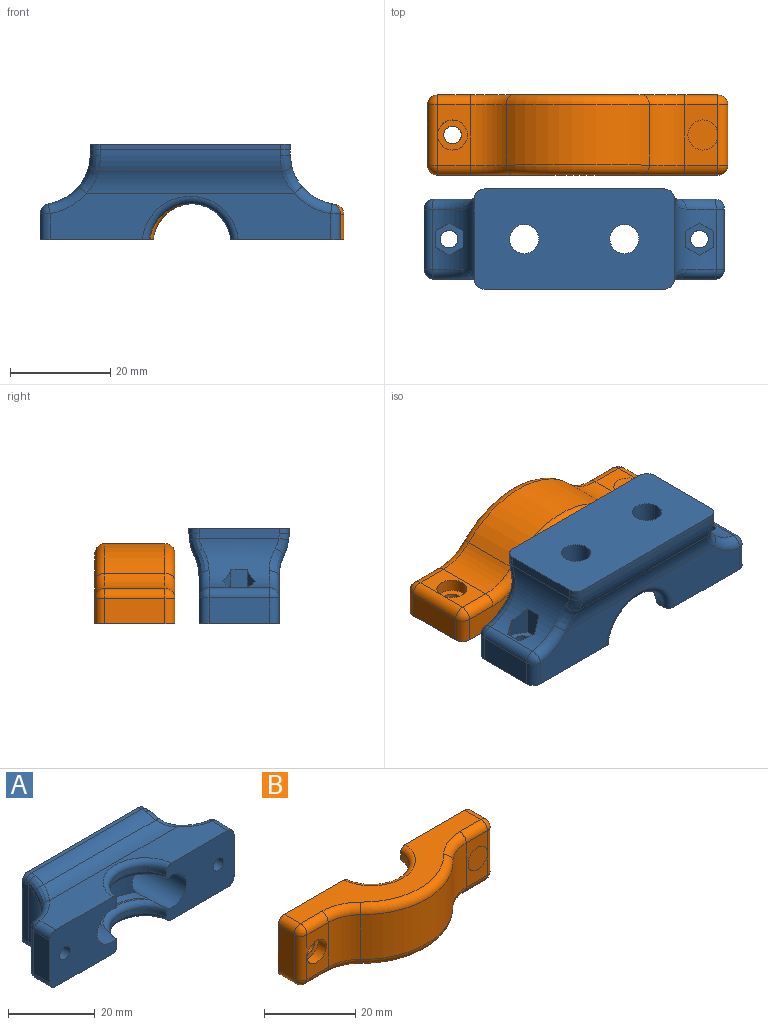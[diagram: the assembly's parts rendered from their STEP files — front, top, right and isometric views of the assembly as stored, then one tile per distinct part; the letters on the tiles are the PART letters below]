
ASSEMBLY  parts=2 mates=1
PART A: 80 faces, bbox 60.1x19.3x20.2 mm
  f0: cylinder r=11.15mm len=12.8mm, axis (0,0,1), area 65.7mm2, adj f5,f6,f76,f78
  f1: plane 14.88x4mm, normal (0,0,1), area 8.4mm2, adj f4,f5,f76,f78
  f2: plane 14.88x4mm, normal (0,0,-1), area 8.4mm2, adj f3,f6,f76,f78
  f3: torus R=9.65mm, axis (0,0,-1), area 49.9mm2, adj f2,f15,f74,f75,f76,f78
  f4: torus R=9.65mm, axis (0,0,1), area 49.9mm2, adj f1,f14,f74,f75,f76,f78
  f5: cone r=10.15mm half-angle=45deg, axis (0,0,1), area 21.1mm2, adj f0,f1,f76,f78
  f6: cone r=11.15mm half-angle=45deg, axis (0,0,-1), area 21.1mm2, adj f0,f2,f76,f78
  f7: cylinder r=2.9mm len=5.8mm, axis (0,1,0), area 72.9mm2, adj f27,f77
  f8: cylinder r=2.9mm len=5.8mm, axis (0,1,0), area 72.9mm2, adj f27,f79
  f9: cylinder r=1.75mm len=5mm, axis (0,1,0), area 55mm2, adj f41,f74
  f10: cylinder r=1.75mm len=5mm, axis (0,1,0), area 55mm2, adj f34,f75
  f11: plane 12x5.17mm, normal (-1,0,0), area 62mm2, adj f19,f20,f59,f75
  f12: plane 12x5.17mm, normal (1,0,0), area 62mm2, adj f21,f22,f67,f74
  f13: plane 56x9.28mm, normal (0,0,-1), area 355mm2, adj f18,f20,f22,f45,f58,f69,f74,f75
  f14: cylinder r=8.15mm len=16.18mm, axis (0,0,1), area 30.7mm2, adj f4,f18,f74,f75
  f15: cylinder r=8.15mm len=16.18mm, axis (0,0,-1), area 30.7mm2, adj f3,f17,f74,f75
  f16: plane 56x9.28mm, normal (0,0,1), area 355mm2, adj f17,f19,f21,f44,f55,f65,f74,f75
  f17: torus R=9.65mm, axis (0,0,-1), area 59.7mm2, adj f15,f16,f74,f75
  f18: torus R=9.65mm, axis (0,0,1), area 59.7mm2, adj f13,f14,f74,f75
  f19: cylinder r=2mm len=5.17mm, axis (0,1,0), area 16.2mm2, adj f11,f16,f57,f75
  f20: cylinder r=2mm len=5.17mm, axis (0,1,0), area 16.2mm2, adj f11,f13,f60,f75
  f21: cylinder r=2mm len=5.17mm, axis (0,-1,0), area 16.2mm2, adj f12,f16,f66,f74
  f22: cylinder r=2mm len=5.17mm, axis (0,-1,0), area 16.2mm2, adj f12,f13,f68,f74
  f23: plane 16x2mm, normal (1,0,0), area 32mm2, adj f27,f47,f61,f62,f72,f73
  f24: plane 36x1mm, normal (0,0,1), area 36mm2, adj f27,f43,f48,f61
  f25: plane 16x2mm, normal (-1,0,0), area 32mm2, adj f27,f46,f48,f49,f50,f52
  f26: plane 36x1mm, normal (0,0,-1), area 36mm2, adj f27,f42,f50,f73
  f27: plane 40x20mm, normal (0,1,0), area 743.7mm2, adj f7,f8,f23,f24,f25,f26,f48,f50
  f28: plane 3.23x2.25mm, normal (1,0,0), area 7.3mm2, adj f29,f33,f34,f46
  f29: plane 3.39x2.85mm, normal (0.5,0,-0.87), area 8.8mm2, adj f28,f30,f34,f46
  f30: plane 5.87x2.93mm, normal (-0.5,0,-0.87), area 14.2mm2, adj f29,f31,f34,f46
  f31: plane 5.74x3.23mm, normal (-1,0,0), area 18.6mm2, adj f30,f32,f34,f46
  f32: plane 5.87x2.93mm, normal (-0.5,0,0.87), area 14.2mm2, adj f31,f33,f34,f46
  f33: plane 3.39x2.85mm, normal (0.5,0,0.87), area 8.8mm2, adj f28,f32,f34,f46
  f34: plane 6.47x5.6mm, normal (0,1,0), area 17.5mm2, adj f10,f28,f29,f30,f31,f32,f33
  f35: plane 5.87x2.93mm, normal (0.5,0,0.87), area 14.2mm2, adj f36,f40,f41,f47
  f36: plane 5.74x3.23mm, normal (1,0,0), area 18.6mm2, adj f35,f37,f41,f47
  f37: plane 5.87x2.93mm, normal (0.5,0,-0.87), area 14.2mm2, adj f36,f38,f41,f47
  f38: plane 3.39x2.85mm, normal (-0.5,0,-0.87), area 8.8mm2, adj f37,f39,f41,f47
  f39: plane 3.23x2.25mm, normal (-1,0,0), area 7.3mm2, adj f38,f40,f41,f47
  f40: plane 3.39x2.85mm, normal (-0.5,0,0.87), area 8.8mm2, adj f35,f39,f41,f47
  f41: plane 6.47x5.6mm, normal (0,1,0), area 17.5mm2, adj f9,f35,f36,f37,f38,f39,f40
  f42: cylinder r=10mm len=36.52mm, axis (-1,0,0), area 163.2mm2, adj f26,f45,f52,f54,f71,f72
  f43: cylinder r=10mm len=36.52mm, axis (1,0,0), area 163.2mm2, adj f24,f44,f49,f51,f62,f63
  f44: cylinder r=10mm len=41.62mm, axis (1,0,0), area 173.6mm2, adj f16,f43,f53,f64
  f45: cylinder r=10mm len=41.62mm, axis (-1,0,0), area 173.6mm2, adj f13,f42,f56,f70
  f46: cylinder r=10mm len=15.87mm, axis (0,0,1), area 146.2mm2, adj f25,f28,f29,f30,f31,f32,f33,f51
  f47: cylinder r=10mm len=15.87mm, axis (0,0,-1), area 146.2mm2, adj f23,f35,f36,f37,f38,f39,f40,f63
  f48: cylinder r=2mm len=2mm, axis (0,1,0), area 3.1mm2, adj f24,f25,f27,f49
  f49: torus R=8mm, axis (1,0,0), area 3.7mm2, adj f25,f43,f48,f51
  f50: cylinder r=2mm len=2mm, axis (0,-1,0), area 3.1mm2, adj f25,f26,f27,f52
  f51: bspline ~6.08x3.25mm, area 8.9mm2, adj f43,f46,f49,f53
  f52: torus R=8mm, axis (1,0,0), area 3.7mm2, adj f25,f42,f50,f54
  f53: bspline ~8.12x5.1mm, area 16.1mm2, adj f44,f46,f51,f55
  f54: bspline ~6.08x3.25mm, area 8.9mm2, adj f42,f46,f52,f56
  f55: torus R=12mm, axis (0,0,-1), area 23.7mm2, adj f16,f46,f53,f57
  f56: bspline ~8.12x5.1mm, area 16.1mm2, adj f45,f46,f54,f58
  f57: sphere r=2mm, area 5.6mm2, adj f19,f55,f59
  f58: torus R=12mm, axis (0,0,1), area 23.7mm2, adj f13,f46,f56,f60
  f59: cylinder r=2mm len=12mm, axis (0,0,1), area 33.7mm2, adj f11,f46,f57,f60
  f60: sphere r=2mm, area 5.6mm2, adj f20,f58,f59
  f61: cylinder r=2mm len=2mm, axis (0,-1,0), area 3.1mm2, adj f23,f24,f27,f62
  f62: torus R=8mm, axis (1,0,0), area 3.7mm2, adj f23,f43,f61,f63
  f63: bspline ~6.08x3.25mm, area 8.9mm2, adj f43,f47,f62,f64
  f64: bspline ~8.12x5.1mm, area 16.1mm2, adj f44,f47,f63,f65
  f65: torus R=12mm, axis (0,0,-1), area 23.7mm2, adj f16,f47,f64,f66
  f66: sphere r=2mm, area 5.6mm2, adj f21,f65,f67
  f67: cylinder r=2mm len=12mm, axis (0,0,-1), area 33.7mm2, adj f12,f47,f66,f68
  f68: sphere r=2mm, area 5.6mm2, adj f22,f67,f69
  f69: torus R=12mm, axis (0,0,1), area 23.7mm2, adj f13,f47,f68,f70
  f70: bspline ~8.12x5.1mm, area 16.1mm2, adj f45,f47,f69,f71
  f71: bspline ~6.08x3.25mm, area 8.9mm2, adj f42,f47,f70,f72
  f72: torus R=8mm, axis (1,0,0), area 3.7mm2, adj f23,f42,f71,f73
  f73: cylinder r=2mm len=2mm, axis (0,1,0), area 3.1mm2, adj f23,f26,f27,f72
  f74: plane 21.97x16.06mm, normal (0,-1,0), area 289.5mm2, adj f3,f4,f9,f12,f13,f14,f15,f16
  f75: plane 21.97x16.06mm, normal (0,-1,0), area 289.5mm2, adj f3,f4,f10,f11,f13,f14,f15,f16
  f76: cylinder r=4.5mm len=15mm, axis (0,1,0), area 348.6mm2, adj f0,f1,f2,f3,f4,f5,f6,f75
  f77: plane 9x9mm, normal (0,-1,0), area 37.2mm2, adj f7,f76
  f78: cylinder r=4.5mm len=15mm, axis (0,1,0), area 348.6mm2, adj f0,f1,f2,f3,f4,f5,f6,f74
  f79: plane 9x9mm, normal (0,-1,0), area 37.2mm2, adj f8,f78
PART B: 49 faces, bbox 60.1x17.9x16.1 mm
  f0: plane 12x6.58mm, normal (0,-1,0), area 78.9mm2, adj f1,f45,f46,f47
  f1: cylinder r=2mm len=12mm, axis (0,0,1), area 37.7mm2, adj f0,f2,f43,f44
  f2: sphere r=2mm, area 6.3mm2, adj f1,f3,f47
  f3: cylinder r=2mm len=5mm, axis (0,-1,0), area 15.7mm2, adj f2,f4,f38,f43
  f4: plane 56x14mm, normal (0,0,1), area 360.4mm2, adj f3,f5,f6,f31,f32,f33,f34,f37
  f5: torus R=12mm, axis (0,0,-1), area 26.8mm2, adj f4,f6,f46,f47
  f6: torus R=18mm, axis (0,0,-1), area 96.3mm2, adj f4,f5,f7,f31
  f7: cylinder r=20mm len=28.57mm, axis (0,0,1), area 381.8mm2, adj f6,f8,f30,f46
  f8: torus R=18mm, axis (0,0,1), area 96.3mm2, adj f7,f9,f10,f29
  f9: torus R=12mm, axis (0,0,1), area 26.8mm2, adj f8,f10,f45,f46
  f10: plane 56x14mm, normal (0,0,-1), area 360.4mm2, adj f8,f9,f11,f17,f18,f28,f29,f34
  f11: cylinder r=2mm len=6.58mm, axis (-1,0,0), area 20.7mm2, adj f10,f12,f16,f29
  f12: plane 12x6.58mm, normal (0,-1,0), area 50.6mm2, adj f11,f13,f30,f32,f48
  f13: cylinder r=2mm len=12mm, axis (0,0,-1), area 37.7mm2, adj f12,f14,f15,f16
  f14: plane 12x5mm, normal (-1,0,0), area 60mm2, adj f13,f28,f33,f34
  f15: sphere r=2mm, area 6.3mm2, adj f13,f32,f33
  f16: sphere r=2mm, area 6.3mm2, adj f11,f13,f28
  f17: cylinder r=2mm len=5mm, axis (0,-1,0), area 15.7mm2, adj f10,f38,f43,f44
  f18: torus R=9.65mm, axis (0,0,1), area 59.7mm2, adj f10,f19,f34,f38
  f19: cylinder r=8.15mm len=16.18mm, axis (0,0,1), area 30.7mm2, adj f18,f20,f34,f38
  f20: torus R=9.65mm, axis (0,0,1), area 59.7mm2, adj f19,f21,f34,f38
  f21: plane 20.2x9.15mm, normal (0,0,1), area 14.5mm2, adj f20,f22,f34,f38
  f22: cone r=10.15mm half-angle=45deg, axis (0,0,1), area 44.5mm2, adj f21,f23,f34,f38
  f23: cylinder r=11.15mm len=22.21mm, axis (0,0,1), area 178.3mm2, adj f22,f24,f34,f38
  f24: cone r=11.15mm half-angle=45deg, axis (0,0,-1), area 44.5mm2, adj f23,f25,f34,f38
  f25: plane 20.2x9.15mm, normal (0,0,-1), area 14.5mm2, adj f24,f26,f34,f38
  f26: torus R=9.65mm, axis (0,0,-1), area 59.7mm2, adj f25,f27,f34,f38
  f27: cylinder r=8.15mm len=16.18mm, axis (0,0,-1), area 30.7mm2, adj f26,f34,f37,f38
  f28: cylinder r=2mm len=5mm, axis (0,1,0), area 15.7mm2, adj f10,f14,f16,f34
  f29: torus R=12mm, axis (0,0,1), area 26.8mm2, adj f8,f10,f11,f30
  f30: cylinder r=10mm len=12mm, axis (0,0,1), area 95.4mm2, adj f7,f12,f29,f31
  f31: torus R=12mm, axis (0,0,-1), area 26.8mm2, adj f4,f6,f30,f32
  f32: cylinder r=2mm len=6.58mm, axis (-1,0,0), area 20.7mm2, adj f4,f12,f15,f31
  f33: cylinder r=2mm len=5mm, axis (0,1,0), area 15.7mm2, adj f4,f14,f15,f34
  f34: plane 21.97x16.06mm, normal (0,1,0), area 316mm2, adj f4,f10,f14,f18,f19,f20,f21,f22
  f35: cylinder r=1.75mm len=4.5mm, axis (0,1,0), area 49.5mm2, adj f34,f36
  f36: plane 6x6mm, normal (0,-1,0), area 18.7mm2, adj f35,f48
  f37: torus R=9.65mm, axis (0,0,-1), area 59.7mm2, adj f4,f27,f34,f38
  f38: plane 21.97x16.06mm, normal (0,1,0), area 316mm2, adj f3,f4,f10,f17,f18,f19,f20,f21
  f39: cylinder r=1.75mm len=4.5mm, axis (0,1,0), area 49.5mm2, adj f38,f40
  f40: plane 6x6mm, normal (0,-1,0), area 18.7mm2, adj f39,f41
  f41: cylinder r=3mm len=6mm, axis (0,-1,0), area 47.1mm2, adj f40,f42
  f42: plane 6x6mm, normal (0,1,0), area 28.3mm2, adj f41
  f43: plane 12x5mm, normal (1,0,0), area 60mm2, adj f1,f3,f17,f38
  f44: sphere r=2mm, area 6.3mm2, adj f1,f17,f45
  f45: cylinder r=2mm len=6.58mm, axis (-1,0,0), area 20.7mm2, adj f0,f9,f10,f44
  f46: cylinder r=10mm len=12mm, axis (0,0,1), area 95.4mm2, adj f0,f5,f7,f9
  f47: cylinder r=2mm len=6.58mm, axis (-1,0,0), area 20.7mm2, adj f0,f2,f4,f5
  f48: cylinder r=3mm len=6mm, axis (0,-1,0), area 47.1mm2, adj f12,f36
PLACE A rot(axis=(1,0,0),90deg) t=(-0.68,-30.47,21.09)mm
PLACE B rot(axis=(-1,0,0),90deg) t=(0,-9.67,-25.92)mm
MATE parallel A.f74 <-> B.f38  axis (0,0,-1) through (19.51,-30.47,-1.41)mm
